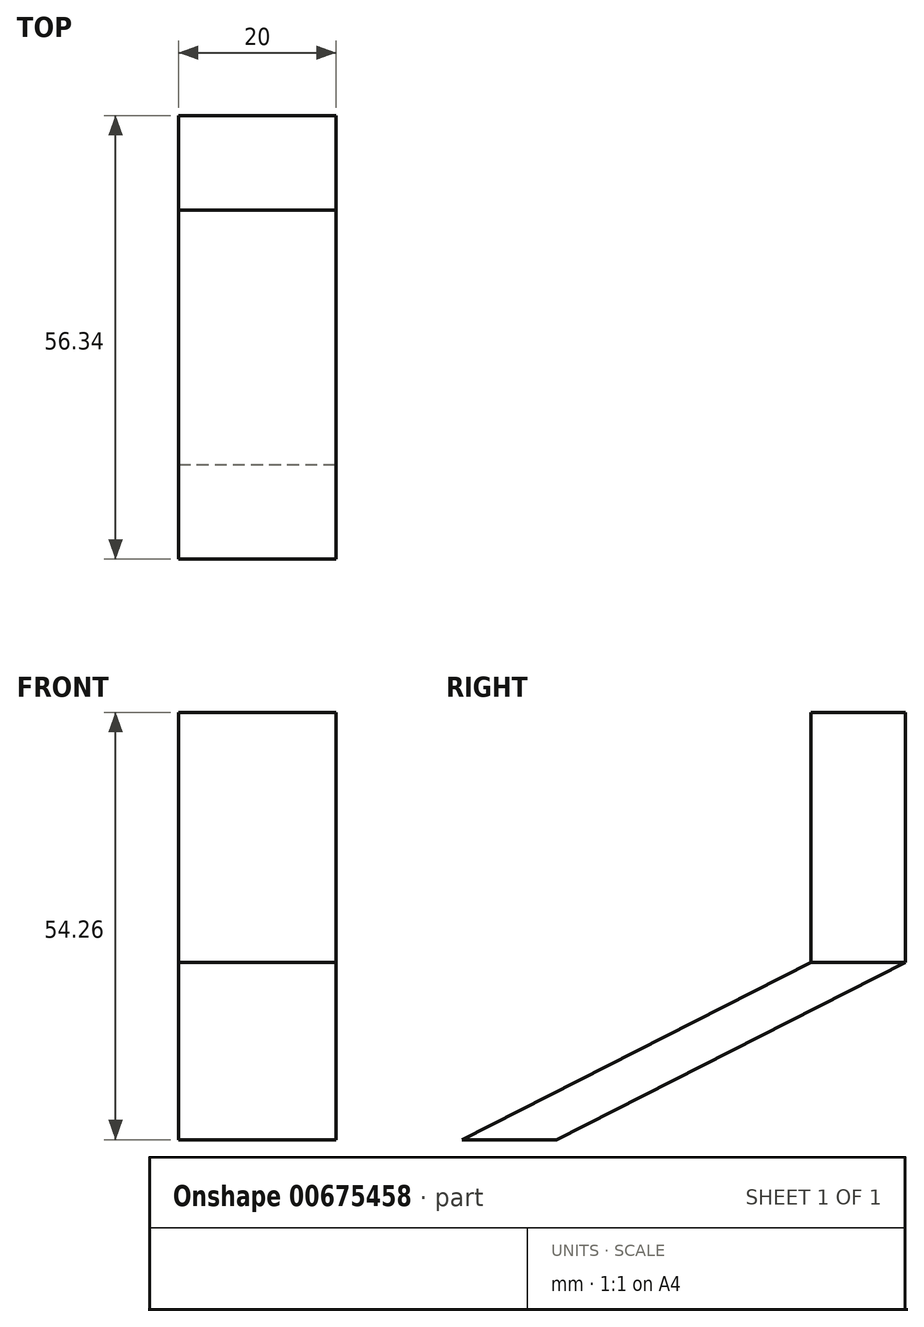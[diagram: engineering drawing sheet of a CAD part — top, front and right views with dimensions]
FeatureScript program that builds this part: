
annotation { "Feature Type Name" : "Feature", "Feature Type Description" : "" }
export const myFeature = defineFeature(function(context is Context, id is Id, definition is map)
    precondition{}
    {
        {
            var Q0;
            Q0=qCreatedBy(makeId("Right.planeOp"),FACE);
            var sketch = newSketch(context, id + "F0", { "sketchPlane" : qUnion([Q0])});
            skLineSegment(sketch, "E0", {"start": v(-44.34, -54.26) * mm, "end": v(0, -31.75) * mm});
            skLineSegment(sketch, "E1", {"start": v(0, -31.75) * mm, "end": v(0, 0) * mm});
            skSolve(sketch);
        }
        {
            var Q0;
            Q0=sQuery(id+"F0.wireOp",EDGE,"E0");
            var Q1;
            Q1=sQuery(id+"F0.wireOp",EDGE,"E1");
            extrude(context, id + "F1", {"bodyType" : ToolBodyType.SURFACE, "surfaceEntities" : qUnion([Q0, Q1]), "depth" : 20 * mm, "offsetDistance" : 25.4 * mm, "hasDraft" : true, "draftAngle" : 3 * degree});
        }
        {
            var Q0;
            Q0=makeQuery(id+"F1.opExtrude","SWEPT_FACE",FACE,{"disambiguationData":[OSD([sQuery(id+"F0.wireOp",EDGE,"E1")])]});
            var Q1;
            Q1=makeQuery(id+"F1.opExtrude","SWEPT_FACE",FACE,{"disambiguationData":[OSD([sQuery(id+"F0.wireOp",EDGE,"E0")])]});
            extrude(context, id + "F2", {"entities" : qUnion([Q0, Q1]), "depth" : 12 * mm, "offsetDistance" : 25.4 * mm});
        }
    });
